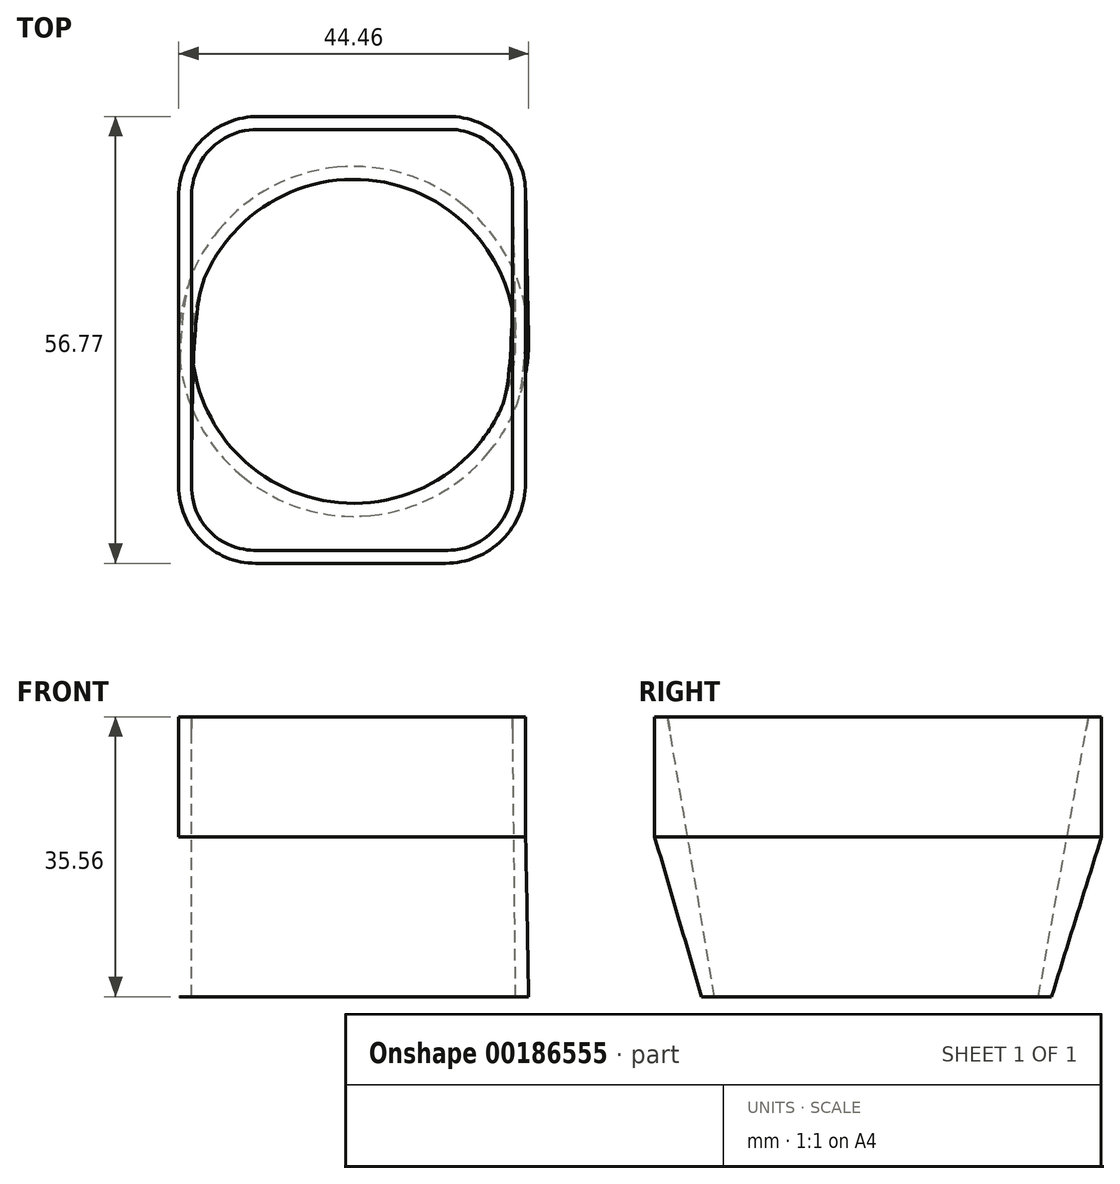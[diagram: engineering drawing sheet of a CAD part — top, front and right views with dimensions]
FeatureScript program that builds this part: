
annotation { "Feature Type Name" : "Feature", "Feature Type Description" : "" }
export const myFeature = defineFeature(function(context is Context, id is Id, definition is map)
    precondition{}
    {
        {
            var Q0;
            Q0=qCreatedBy(makeId("Top.planeOp"),FACE);
            var sketch = newSketch(context, id + "F0", { "sketchPlane" : qUnion([Q0])});
            skCircle(sketch, "E0", {"center": v(0, 0) * mm, "radius": 22.23 * mm});
            skPoint(sketch, "E1", {"position": v(0, -22.23) * mm});
            skPoint(sketch, "E2", {"position": v(-22.23, 0) * mm});
            skPoint(sketch, "E3", {"position": v(0, 22.23) * mm});
            skPoint(sketch, "E4", {"position": v(22.23, 0) * mm});
            skSolve(sketch);
        }
        {
            var Q0;
            Q0=qCreatedBy(makeId("Top.planeOp"),FACE);
            cPlane(context, id + "F1", {"entities" : qUnion([Q0]), "cplaneType" : CPlaneType.OFFSET, "offset" : 20.32 * mm, "width" : 152.4 * mm, "height" : 152.4 * mm});
        }
        {
            var Q0;
            Q0=qCreatedBy(id+"F1.planeOp",FACE);
            var sketch = newSketch(context, id + "F2", { "sketchPlane" : qUnion([Q0])});
            skLineSegment(sketch, "E5", {"start": v(21.84, -18.03) * mm, "end": v(21.84, 18.8) * mm});
            skLineSegment(sketch, "E6", {"start": v(11.68, -28.2) * mm, "end": v(-12.45, -28.2) * mm});
            skLineSegment(sketch, "E7", {"start": v(-22.23, -18.41) * mm, "end": v(-22.23, 18.41) * mm});
            skLineSegment(sketch, "E8", {"start": v(-12.07, 28.57) * mm, "end": v(12.06, 28.57) * mm});
            skArc(sketch, "E9", {"start": v(11.68, -28.2) * mm, "mid": v(18.87, -25.22) * mm, "end": v(21.84, -18.03) * mm});
            skArc(sketch, "E10", {"start": v(-22.23, -18.41) * mm, "mid": v(-19.36, -25.33) * mm, "end": v(-12.45, -28.2) * mm});
            skArc(sketch, "E11", {"start": v(-12.07, 28.57) * mm, "mid": v(-19.25, 25.6) * mm, "end": v(-22.23, 18.41) * mm});
            skArc(sketch, "E12", {"start": v(21.84, 18.8) * mm, "mid": v(18.98, 25.71) * mm, "end": v(12.06, 28.57) * mm});
            skPoint(sketch, "E13", {"position": v(0, 0) * mm});
            skSolve(sketch);
        }
        {
            var Q0;
            Q0 = qSketchRegion(id + "F2", true);
            var Q1;
            Q1 = qSketchRegion(id + "F0", true);
            loft(context, id + "F3", {"sheetProfilesArray" : [{ "sheetProfileEntities" : qUnion([Q0]) }, { "sheetProfileEntities" : qUnion([Q1]) }]});
        }
        {
            var Q0;
            Q0=makeQuery(id+"F3.opLoft","CAP_FACE",FACE,{"disambiguationData":[OSD([makeQuery(id+"F2.imprint","IMPRINT",FACE,{"disambiguationData":[TD([[makeQuery(id+"F2.imprint","IMPRINT",EDGE,{"derivedFrom":sQuery(id+"F2.wireOp",EDGE,"E5")}),1.0]])]})])],"isStart":true});
            extrude(context, id + "F4", {"entities" : qUnion([Q0]), "operationType" : NewBodyOperationType.ADD, "depth" : 15.24 * mm});
        }
        {
            var Q0;
            Q0=makeQuery(id+"F3.opLoft","CAP_FACE",FACE,{"disambiguationData":[OSD([makeQuery(id+"F0.imprint","IMPRINT",FACE,{"disambiguationData":[TD([[makeQuery(id+"F0.imprint","IMPRINT",EDGE,{"derivedFrom":sQuery(id+"F0.wireOp",EDGE,"E0")}),1.0]])]})])],"isStart":true});
            var sketch = newSketch(context, id + "F5", { "sketchPlane" : qUnion([Q0])});
            skCircle(sketch, "E14", {"center": v(0, 0) * mm, "radius": 20.57 * mm});
            skSolve(sketch);
        }
        {
            var Q0;
            Q0=makeQuery(id+"F4.opExtrude","CAP_FACE",FACE,{"disambiguationData":[OSD([makeQuery(id+"F2.imprint","IMPRINT",FACE,{"disambiguationData":[TD([[makeQuery(id+"F2.imprint","IMPRINT",EDGE,{"derivedFrom":sQuery(id+"F2.wireOp",EDGE,"E5")}),1.0]])]})])],"isStart":false});
            var sketch = newSketch(context, id + "F6", { "sketchPlane" : qUnion([Q0])});
            skFitSpline(sketch, "E15.0", {"points": [v(-20.57, 18.41) * mm, v(-20.57, 18.7) * mm, v(-20.55, 19.25) * mm, v(-20.42, 20.08) * mm, v(-20.22, 20.89) * mm, v(-19.85, 21.94) * mm, v(-19.19, 23.17) * mm, v(-18.12, 24.47) * mm, v(-16.82, 25.54) * mm, v(-15.34, 26.33) * mm, v(-14, 26.73) * mm, v(-12.9, 26.9) * mm, v(-12.34, 26.92) * mm, v(-12.07, 26.92) * mm]});
            skFitSpline(sketch, "E15.1", {"points": [v(-20.57, -18.41) * mm, v(-20.57, -6.14) * mm, v(-20.57, 6.14) * mm, v(-20.57, 18.41) * mm]});
            skFitSpline(sketch, "E15.2", {"points": [v(-12.07, 26.92) * mm, v(-4.02, 26.92) * mm, v(4.02, 26.92) * mm, v(12.06, 26.92) * mm]});
            skFitSpline(sketch, "E15.3", {"points": [v(-12.45, -26.54) * mm, v(-12.71, -26.54) * mm, v(-13.24, -26.52) * mm, v(-14.03, -26.4) * mm, v(-14.8, -26.2) * mm, v(-15.81, -25.85) * mm, v(-17, -25.22) * mm, v(-18.23, -24.2) * mm, v(-19.25, -22.96) * mm, v(-20, -21.55) * mm, v(-20.4, -20.27) * mm, v(-20.55, -19.21) * mm, v(-20.57, -18.68) * mm, v(-20.57, -18.41) * mm]});
            skFitSpline(sketch, "E15.4", {"points": [v(12.06, 26.92) * mm, v(12.33, 26.92) * mm, v(12.86, 26.9) * mm, v(13.65, 26.78) * mm, v(14.43, 26.59) * mm, v(15.43, 26.23) * mm, v(16.61, 25.6) * mm, v(17.85, 24.58) * mm, v(18.87, 23.34) * mm, v(19.62, 21.93) * mm, v(20.01, 20.65) * mm, v(20.17, 19.6) * mm, v(20.2, 19.06) * mm, v(20.2, 18.8) * mm]});
            skFitSpline(sketch, "E15.5", {"points": [v(20.2, 18.8) * mm, v(20.2, 6.52) * mm, v(20.2, -5.76) * mm, v(20.2, -18.03) * mm]});
            skFitSpline(sketch, "E15.6", {"points": [v(20.2, -18.03) * mm, v(20.2, -18.31) * mm, v(20.17, -18.87) * mm, v(20.04, -19.7) * mm, v(19.84, -20.5) * mm, v(19.46, -21.56) * mm, v(18.8, -22.8) * mm, v(17.74, -24.09) * mm, v(16.44, -25.15) * mm, v(14.96, -25.95) * mm, v(13.62, -26.35) * mm, v(12.52, -26.52) * mm, v(11.96, -26.54) * mm, v(11.68, -26.54) * mm]});
            skFitSpline(sketch, "E15.7", {"points": [v(11.68, -26.54) * mm, v(3.64, -26.54) * mm, v(-4.4, -26.54) * mm, v(-12.45, -26.54) * mm]});
            skSolve(sketch);
        }
        {
            var Q1;
            Q1 = qSketchRegion(id + "F5", true);
            var Q2;
            Q2 = qSketchRegion(id + "F6", true);
            loft(context, id + "F7", {"operationType" : NewBodyOperationType.REMOVE, "sheetProfilesArray" : [{ "sheetProfileEntities" : qUnion([Q1]) }, { "sheetProfileEntities" : qUnion([Q2]) }]});
        }
    });
